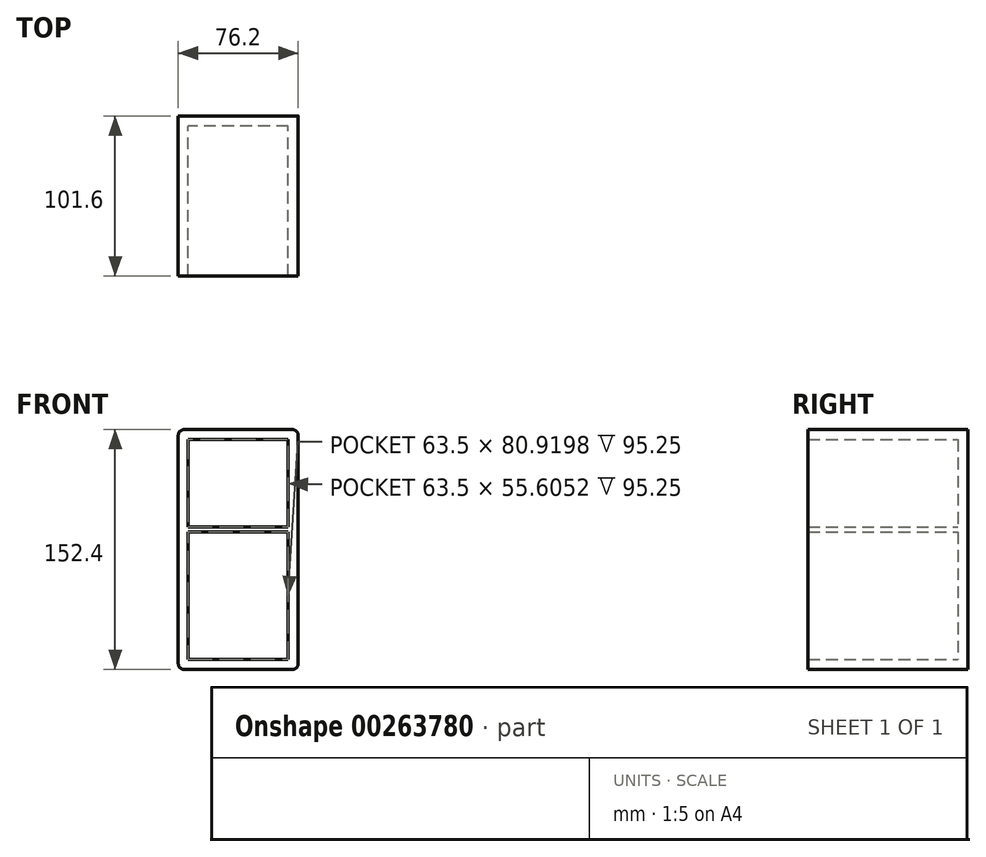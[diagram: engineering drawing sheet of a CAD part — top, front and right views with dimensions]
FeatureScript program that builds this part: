
annotation { "Feature Type Name" : "Feature", "Feature Type Description" : "" }
export const myFeature = defineFeature(function(context is Context, id is Id, definition is map)
    precondition{}
    {
        {
            var Q0;
            Q0=qCreatedBy(makeId("Front.planeOp"),FACE);
            var sketch = newSketch(context, id + "F0", { "sketchPlane" : qUnion([Q0])});
            skLineSegment(sketch, "E0.bottom", {"start": v(-34.29, 76.2) * mm, "end": v(34.3, 76.2) * mm});
            skLineSegment(sketch, "E0.top", {"start": v(-34.3, -76.2) * mm, "end": v(34.29, -76.2) * mm});
            skLineSegment(sketch, "E0.left", {"start": v(-38.1, 72.4) * mm, "end": v(-38.1, -72.4) * mm});
            skLineSegment(sketch, "E0.right", {"start": v(38.1, 72.4) * mm, "end": v(38.1, -72.4) * mm});
            skPoint(sketch, "E0.middle", {"position": v(0, 0) * mm});
            skPoint(sketch, "E1.visualSharp", {"position": v(-38.1, 76.2) * mm});
            skArc(sketch, "E1.filletArc", {"start": v(-34.29, 76.2) * mm, "mid": v(-36.98, 75.08) * mm, "end": v(-38.1, 72.4) * mm});
            skPoint(sketch, "E2.visualSharp", {"position": v(38.1, 76.2) * mm});
            skArc(sketch, "E2.filletArc", {"start": v(38.1, 72.4) * mm, "mid": v(36.98, 75.08) * mm, "end": v(34.3, 76.2) * mm});
            skPoint(sketch, "E3.visualSharp", {"position": v(-38.1, -76.2) * mm});
            skArc(sketch, "E3.filletArc", {"start": v(-38.1, -72.4) * mm, "mid": v(-36.98, -75.08) * mm, "end": v(-34.3, -76.2) * mm});
            skPoint(sketch, "E4.visualSharp", {"position": v(38.1, -76.2) * mm});
            skArc(sketch, "E4.filletArc", {"start": v(34.29, -76.2) * mm, "mid": v(36.98, -75.08) * mm, "end": v(38.1, -72.4) * mm});
            skSolve(sketch);
        }
        {
            var Q0;
            Q0=makeQuery(id+"F0.imprint","IMPRINT",FACE,{"disambiguationData":[TD([[makeQuery(id+"F0.imprint","IMPRINT",EDGE,{"derivedFrom":sQuery(id+"F0.wireOp",EDGE,"E0.bottom")}),-1.0]])]});
            extrude(context, id + "F1", {"entities" : qUnion([Q0]), "depth" : 101.6 * mm});
        }
        {
            var Q0;
            Q0=makeQuery(id+"F1.opExtrude","CAP_FACE",FACE,{"disambiguationData":[OSD([sQuery(id+"F0.wireOp",EDGE,"E0.bottom"),sQuery(id+"F0.wireOp",EDGE,"E0.top"),sQuery(id+"F0.wireOp",EDGE,"E0.left"),sQuery(id+"F0.wireOp",EDGE,"E0.right"),sQuery(id+"F0.wireOp",EDGE,"E1.filletArc"),sQuery(id+"F0.wireOp",EDGE,"E2.filletArc"),sQuery(id+"F0.wireOp",EDGE,"E3.filletArc"),sQuery(id+"F0.wireOp",EDGE,"E4.filletArc")])],"isStart":false});
            shell(context, id + "F2", {"entities" : qUnion([Q0]), "thickness" : 6.35 * mm});
        }
        {
            var Q0;
            Q0=makeQuery(id+"F2.opShell","OFFSET_FACE",FACE,{"disambiguationData":[OSD([sQuery(id+"F0.wireOp",EDGE,"E0.bottom"),sQuery(id+"F0.wireOp",EDGE,"E0.top"),sQuery(id+"F0.wireOp",EDGE,"E0.left"),sQuery(id+"F0.wireOp",EDGE,"E0.right"),sQuery(id+"F0.wireOp",EDGE,"E1.filletArc"),sQuery(id+"F0.wireOp",EDGE,"E2.filletArc"),sQuery(id+"F0.wireOp",EDGE,"E3.filletArc"),sQuery(id+"F0.wireOp",EDGE,"E4.filletArc")])]});
            var sketch = newSketch(context, id + "F3", { "sketchPlane" : qUnion([Q0])});
            skLineSegment(sketch, "E5.bottom", {"start": v(31.75, 14.24) * mm, "end": v(-31.75, 14.24) * mm});
            skLineSegment(sketch, "E5.top", {"start": v(31.75, 11.07) * mm, "end": v(-31.75, 11.07) * mm});
            skLineSegment(sketch, "E5.left", {"start": v(31.75, 14.24) * mm, "end": v(31.75, 11.07) * mm});
            skLineSegment(sketch, "E5.right", {"start": v(-31.75, 14.24) * mm, "end": v(-31.75, 11.07) * mm});
            skPoint(sketch, "E5.middle", {"position": v(0, 12.66) * mm});
            skSolve(sketch);
        }
        {
            var Q0;
            {var subQ0=sQuery(id+"F3.wireOp",EDGE,"E5.left");Q0=makeQuery(id+"F3.imprint","IMPRINT",FACE,{"disambiguationData":[TD([[makeQuery(id+"F3.imprint","IMPRINT",EDGE,{"derivedFrom":subQ0}),-1.0]])]});}
            var Q1;
            {var subQ0=sQuery(id+"F3.wireOp",EDGE,"E5.right");Q1=makeQuery(id+"F3.imprint","IMPRINT",FACE,{"disambiguationData":[TD([[makeQuery(id+"F3.imprint","IMPRINT",EDGE,{"derivedFrom":subQ0}),1.0]])]});}
            extrude(context, id + "F4", {"entities" : qUnion([Q0, Q1]), "operationType" : NewBodyOperationType.ADD, "depth" : 95.25 * mm});
        }
    });
